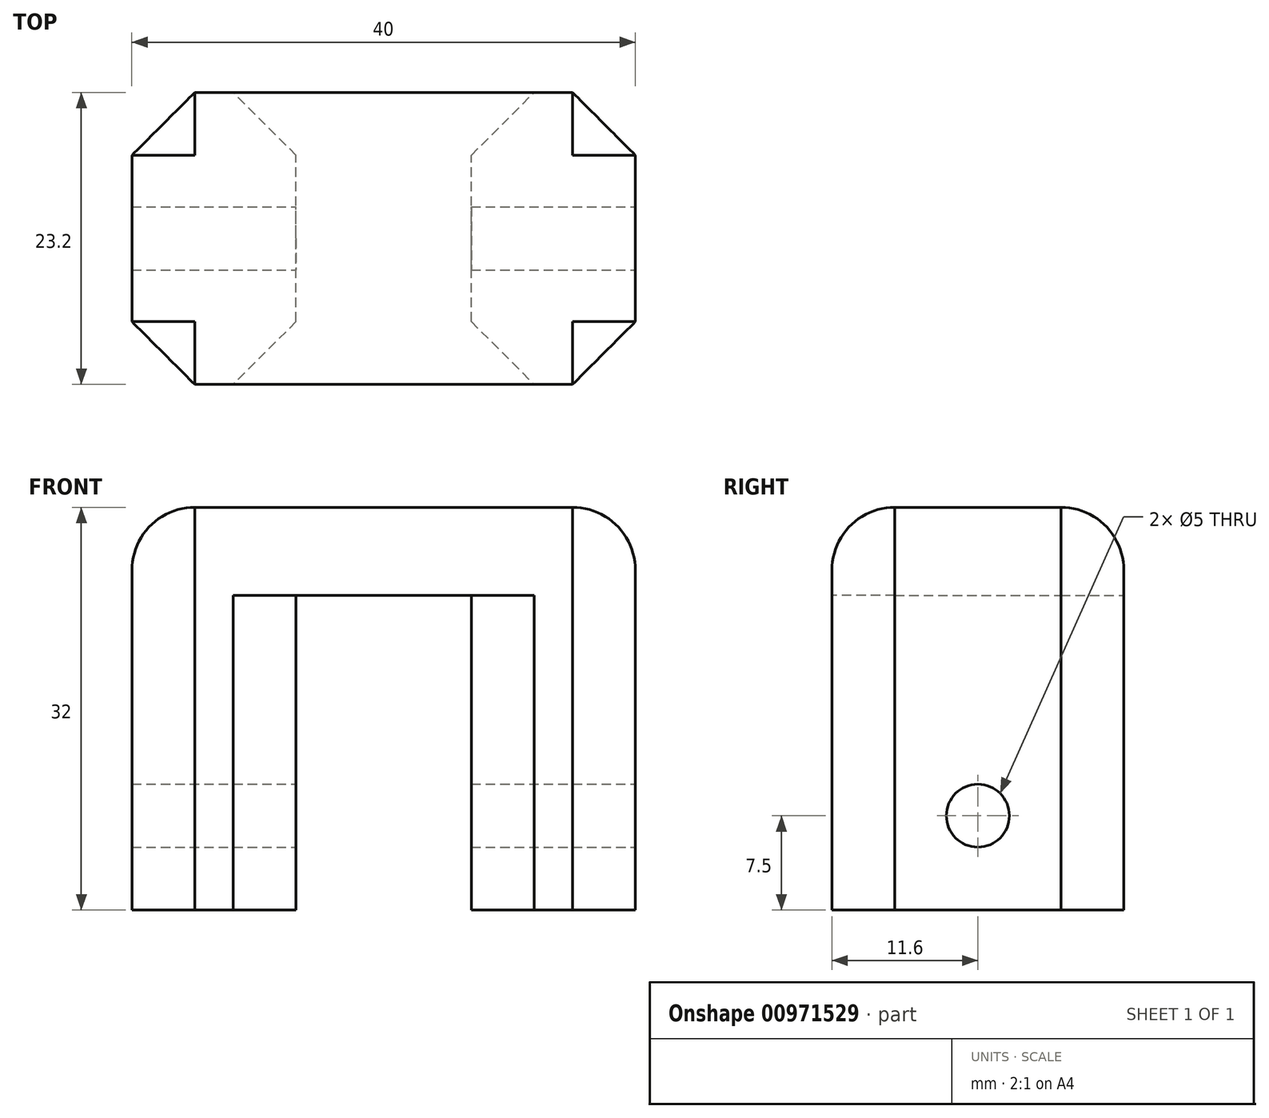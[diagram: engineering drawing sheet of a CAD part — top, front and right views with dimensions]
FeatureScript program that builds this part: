
annotation { "Feature Type Name" : "Feature", "Feature Type Description" : "" }
export const myFeature = defineFeature(function(context is Context, id is Id, definition is map)
    precondition{}
    {
        {
            var Q0;
            Q0=qCreatedBy(makeId("Front.planeOp"),FACE);
            var sketch = newSketch(context, id + "F0", { "sketchPlane" : qUnion([Q0])});
            skLineSegment(sketch, "E0", {"start": v(-41.09, -25) * mm, "end": v(-28.05, -25) * mm});
            skLineSegment(sketch, "E1", {"start": v(-28.05, -25) * mm, "end": v(-28.05, 0) * mm});
            skLineSegment(sketch, "E2", {"start": v(-28.05, 0) * mm, "end": v(-14.13, 0) * mm});
            skLineSegment(sketch, "E3", {"start": v(-14.13, 0) * mm, "end": v(-14.13, -25) * mm});
            skLineSegment(sketch, "E4", {"start": v(-14.13, -25) * mm, "end": v(-1.09, -25) * mm});
            skLineSegment(sketch, "E5", {"start": v(-1.09, -25) * mm, "end": v(-1.09, 7) * mm});
            skLineSegment(sketch, "E6", {"start": v(-1.09, 7) * mm, "end": v(-41.09, 7) * mm});
            skLineSegment(sketch, "E7", {"start": v(-41.09, 7) * mm, "end": v(-41.09, -25) * mm});
            skSolve(sketch);
        }
        {
            var Q0;
            Q0=qSketchRegion(id+"F0",true);
            var Q1;
            Q1=sQuery(id+"F0.wireOp",EDGE,"E6");
            var Q2;
            Q2=sQuery(id+"F0.wireOp",EDGE,"E5");
            var Q3;
            Q3=sQuery(id+"F0.wireOp",EDGE,"E3");
            var Q4;
            Q4=sQuery(id+"F0.wireOp",EDGE,"E2");
            var Q5;
            Q5=sQuery(id+"F0.wireOp",EDGE,"E1");
            var Q6;
            Q6=sQuery(id+"F0.wireOp",EDGE,"E7");
            var Q7;
            Q7=sQuery(id+"F0.wireOp",EDGE,"E0");
            var Q8;
            Q8=sQuery(id+"F0.wireOp",EDGE,"E4");
            extrude(context, id + "F1", {"entities" : qUnion([Q0]), "surfaceEntities" : qUnion([Q1, Q2, Q3, Q4, Q5, Q6, Q7, Q8]), "endBound" : BoundingType.SYMMETRIC, "depth" : 23.2 * mm, "offsetDistance" : 25 * mm});
        }
        {
            var Q0;
            Q0=makeQuery(id+"F1.opExtrude","SWEPT_FACE",FACE,{"disambiguationData":[OSD([sQuery(id+"F0.wireOp",EDGE,"E5")])]});
            var sketch = newSketch(context, id + "F2", { "sketchPlane" : qUnion([Q0])});
            skCircle(sketch, "E8", {"center": v(0, -17.5) * mm, "radius": 2.5 * mm});
            skSolve(sketch);
        }
        {
            var Q0;
            Q0=qSketchRegion(id+"F2",true);
            extrude(context, id + "F3", {"entities" : qUnion([Q0]), "operationType" : NewBodyOperationType.REMOVE, "oppositeDirection" : true, "depth" : 107 * mm, "offsetDistance" : 25 * mm});
        }
        {
            var Q0;
            Q0=makeQuery(id+"F1.opExtrude","SWEPT_EDGE",EDGE,{"disambiguationData":[OSD([sQuery(id+"F0.wireOp",EDGE,"E5"),sQuery(id+"F0.wireOp",EDGE,"E6")])]});
            var Q1;
            Q1=makeQuery(id+"F1.opExtrude","SWEPT_EDGE",EDGE,{"disambiguationData":[OSD([sQuery(id+"F0.wireOp",EDGE,"E6"),sQuery(id+"F0.wireOp",EDGE,"E7")])]});
            var Q2;
            Q2=makeQuery(id+"F1.opExtrude","CAP_EDGE",EDGE,{"disambiguationData":[OSD([sQuery(id+"F0.wireOp",EDGE,"E6")])],"isStart":true});
            var Q3;
            Q3=makeQuery(id+"F1.opExtrude","CAP_EDGE",EDGE,{"disambiguationData":[OSD([sQuery(id+"F0.wireOp",EDGE,"E6")])],"isStart":false});
            fillet(context, id + "F4", {"entities" : qUnion([Q0, Q1, Q2, Q3]), "radius" : 5 * mm, "tangentPropagation" : true, "allowEdgeOverflow" : false});
        }
        {
            var Q0;
            Q0=makeQuery(id+"F1.opExtrude","CAP_EDGE",EDGE,{"disambiguationData":[OSD([sQuery(id+"F0.wireOp",EDGE,"E5")])],"isStart":true});
            var Q1;
            Q1=makeQuery(id+"F1.opExtrude","CAP_EDGE",EDGE,{"disambiguationData":[OSD([sQuery(id+"F0.wireOp",EDGE,"E5")])],"isStart":false});
            var Q2;
            Q2=makeQuery(id+"F1.opExtrude","CAP_EDGE",EDGE,{"disambiguationData":[OSD([sQuery(id+"F0.wireOp",EDGE,"E3")])],"isStart":false});
            var Q3;
            Q3=makeQuery(id+"F1.opExtrude","CAP_EDGE",EDGE,{"disambiguationData":[OSD([sQuery(id+"F0.wireOp",EDGE,"E3")])],"isStart":true});
            var Q4;
            Q4=makeQuery(id+"F1.opExtrude","CAP_EDGE",EDGE,{"disambiguationData":[OSD([sQuery(id+"F0.wireOp",EDGE,"E7")])],"isStart":false});
            var Q5;
            Q5=makeQuery(id+"F1.opExtrude","CAP_EDGE",EDGE,{"disambiguationData":[OSD([sQuery(id+"F0.wireOp",EDGE,"E7")])],"isStart":true});
            var Q6;
            Q6=makeQuery(id+"F1.opExtrude","CAP_EDGE",EDGE,{"disambiguationData":[OSD([sQuery(id+"F0.wireOp",EDGE,"E1")])],"isStart":true});
            var Q7;
            Q7=makeQuery(id+"F1.opExtrude","CAP_EDGE",EDGE,{"disambiguationData":[OSD([sQuery(id+"F0.wireOp",EDGE,"E1")])],"isStart":false});
            chamfer(context, id + "F5", {"entities" : qUnion([Q0, Q1, Q2, Q3, Q4, Q5, Q6, Q7]), "width" : 5 * mm, "tangentPropagation" : true});
        }
    });
